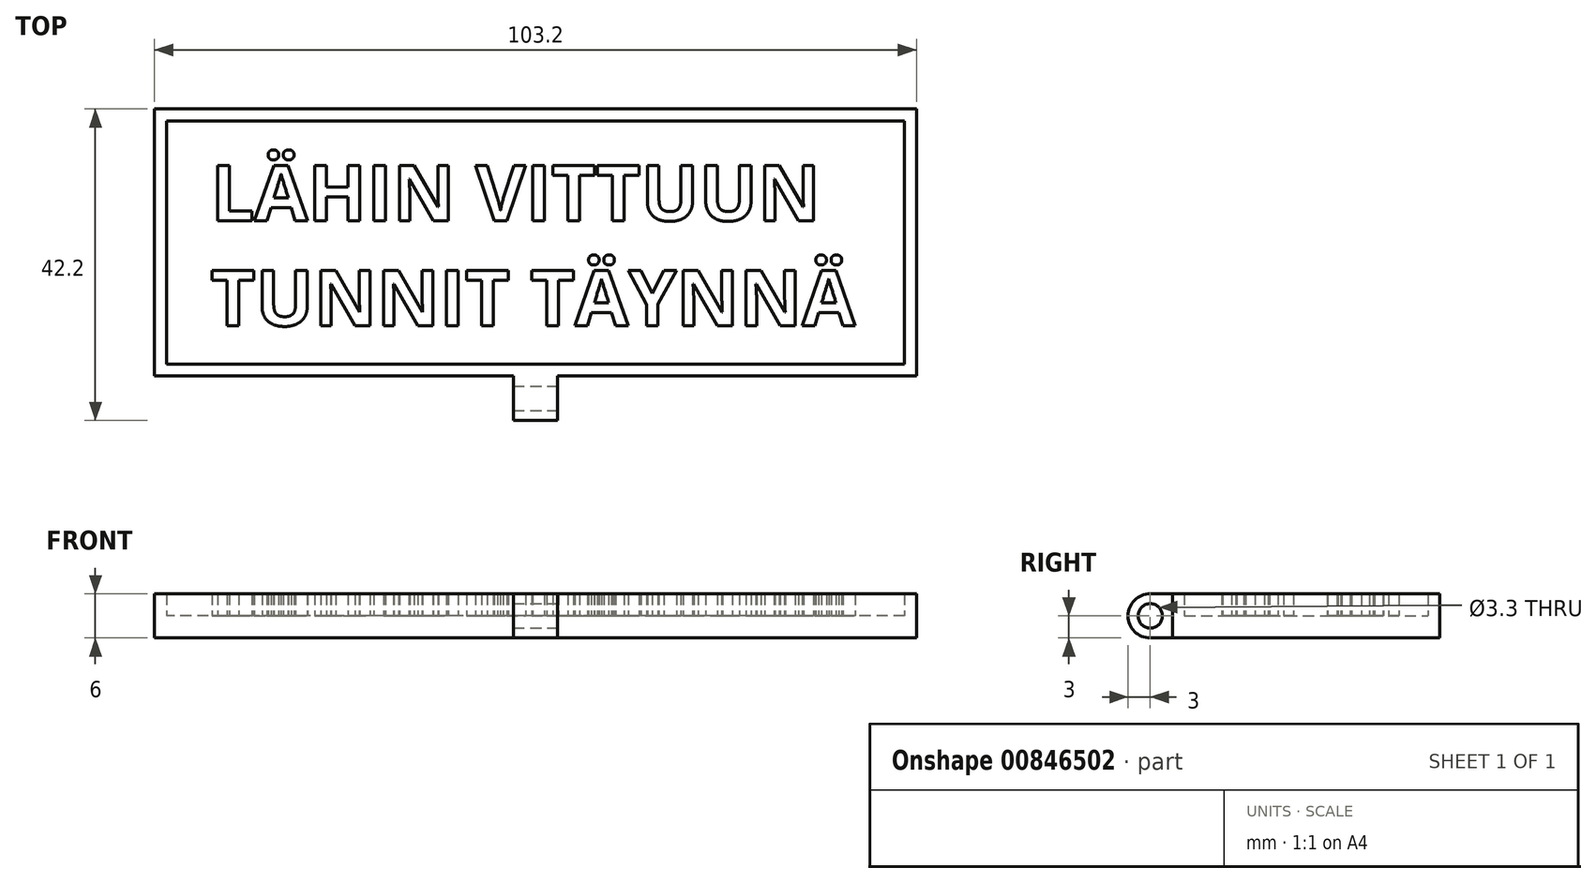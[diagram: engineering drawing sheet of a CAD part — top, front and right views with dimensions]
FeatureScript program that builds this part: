
annotation { "Feature Type Name" : "Feature", "Feature Type Description" : "" }
export const myFeature = defineFeature(function(context is Context, id is Id, definition is map)
    precondition{}
    {
        {
            var Q0;
            Q0=qCreatedBy(makeId("Top.planeOp"),FACE);
            var sketch = newSketch(context, id + "F0", { "sketchPlane" : qUnion([Q0])});
            skText(sketch, "E0", { "text": "LÄHIN VITTUUN\nTUNNIT TÄYNNÄ", "fontName": "OpenSans-Bold.ttf"});
            skLineSegment(sketch, "E1.bottom", {"start": v(0, 0) * mm, "end": v(100, 0) * mm});
            skLineSegment(sketch, "E1.top", {"start": v(0, -33) * mm, "end": v(100, -33) * mm});
            skLineSegment(sketch, "E1.left", {"start": v(0, 0) * mm, "end": v(0, -33) * mm});
            skLineSegment(sketch, "E1.right", {"start": v(100, 0) * mm, "end": v(100, -33) * mm});
            skLineSegment(sketch, "E2.0", {"start": v(-1.6, 1.6) * mm, "end": v(-1.6, -34.6) * mm});
            skLineSegment(sketch, "E2.1", {"start": v(-1.6, 1.6) * mm, "end": v(101.6, 1.6) * mm});
            skLineSegment(sketch, "E2.2", {"start": v(101.6, 1.6) * mm, "end": v(101.6, -34.6) * mm});
            skLineSegment(sketch, "E2.3", {"start": v(-1.6, -34.6) * mm, "end": v(101.6, -34.6) * mm});
            const initialGuessF0  = {"E0": [0.006, -0.01354, 1, 0, 0.00754]};
            skSetInitialGuess(sketch, initialGuessF0);
            skSolve(sketch);
        }
        {
            var Q0;
            Q0=makeQuery(id+"F0.imprint","IMPRINT",FACE,{"disambiguationData":[TD([[makeQuery(id+"F0.imprint","IMPRINT",EDGE,{"derivedFrom":sQuery(id+"F0.wireOp",EDGE,"E1.bottom")}),1.0]])]});
            var Q1;
            Q1=makeQuery(id+"F0.imprint","IMPRINT",FACE,{"disambiguationData":[TD([[makeQuery(id+"F0.imprint","IMPRINT",EDGE,{"derivedFrom":sQuery(id+"F0.wireOp",EDGE,"E0.sketch_text.stroke-0")}),-1.0]])]});
            var Q2;
            Q2=makeQuery(id+"F0.imprint","IMPRINT",FACE,{"disambiguationData":[TD([[makeQuery(id+"F0.imprint","IMPRINT",EDGE,{"derivedFrom":sQuery(id+"F0.wireOp",EDGE,"E0.sketch_text.stroke-0")}),1.0]])]});
            var Q3;
            Q3=makeQuery(id+"F0.imprint","IMPRINT",FACE,{"disambiguationData":[TD([[makeQuery(id+"F0.imprint","IMPRINT",EDGE,{"derivedFrom":sQuery(id+"F0.wireOp",EDGE,"E0.sketch_text.stroke-109")}),-1.0]])]});
            var Q4;
            Q4=makeQuery(id+"F0.imprint","IMPRINT",FACE,{"disambiguationData":[TD([[makeQuery(id+"F0.imprint","IMPRINT",EDGE,{"derivedFrom":sQuery(id+"F0.wireOp",EDGE,"E0.sketch_text.stroke-86")}),-1.0]])]});
            var Q5;
            Q5=makeQuery(id+"F0.imprint","IMPRINT",FACE,{"disambiguationData":[TD([[makeQuery(id+"F0.imprint","IMPRINT",EDGE,{"derivedFrom":sQuery(id+"F0.wireOp",EDGE,"E0.sketch_text.stroke-78")}),-1.0]])]});
            var Q6;
            Q6=makeQuery(id+"F0.imprint","IMPRINT",FACE,{"disambiguationData":[TD([[makeQuery(id+"F0.imprint","IMPRINT",EDGE,{"derivedFrom":sQuery(id+"F0.wireOp",EDGE,"E0.sketch_text.stroke-64")}),-1.0]])]});
            var Q7;
            Q7=makeQuery(id+"F0.imprint","IMPRINT",FACE,{"disambiguationData":[TD([[makeQuery(id+"F0.imprint","IMPRINT",EDGE,{"derivedFrom":sQuery(id+"F0.wireOp",EDGE,"E0.sketch_text.stroke-94")}),-1.0]])]});
            var Q8;
            Q8=makeQuery(id+"F0.imprint","IMPRINT",FACE,{"disambiguationData":[TD([[makeQuery(id+"F0.imprint","IMPRINT",EDGE,{"derivedFrom":sQuery(id+"F0.wireOp",EDGE,"E0.sketch_text.stroke-74")}),-1.0]])]});
            var Q9;
            Q9=makeQuery(id+"F0.imprint","IMPRINT",FACE,{"disambiguationData":[TD([[makeQuery(id+"F0.imprint","IMPRINT",EDGE,{"derivedFrom":sQuery(id+"F0.wireOp",EDGE,"E0.sketch_text.stroke-6")}),-1.0]])]});
            var Q10;
            Q10=makeQuery(id+"F0.imprint","IMPRINT",FACE,{"disambiguationData":[TD([[makeQuery(id+"F0.imprint","IMPRINT",EDGE,{"derivedFrom":sQuery(id+"F0.wireOp",EDGE,"E0.sketch_text.stroke-146")}),-1.0]])]});
            var Q11;
            Q11=makeQuery(id+"F0.imprint","IMPRINT",FACE,{"disambiguationData":[TD([[makeQuery(id+"F0.imprint","IMPRINT",EDGE,{"derivedFrom":sQuery(id+"F0.wireOp",EDGE,"E0.sketch_text.stroke-18")}),-1.0]])]});
            var Q12;
            Q12=makeQuery(id+"F0.imprint","IMPRINT",FACE,{"disambiguationData":[TD([[makeQuery(id+"F0.imprint","IMPRINT",EDGE,{"derivedFrom":sQuery(id+"F0.wireOp",EDGE,"E0.sketch_text.stroke-246")}),-1.0]])]});
            var Q13;
            Q13=makeQuery(id+"F0.imprint","IMPRINT",FACE,{"disambiguationData":[TD([[makeQuery(id+"F0.imprint","IMPRINT",EDGE,{"derivedFrom":sQuery(id+"F0.wireOp",EDGE,"E0.sketch_text.stroke-14")}),1.0]])]});
            var Q14;
            Q14=makeQuery(id+"F0.imprint","IMPRINT",FACE,{"disambiguationData":[TD([[makeQuery(id+"F0.imprint","IMPRINT",EDGE,{"derivedFrom":sQuery(id+"F0.wireOp",EDGE,"E0.sketch_text.stroke-34")}),-1.0]])]});
            var Q15;
            Q15=makeQuery(id+"F0.imprint","IMPRINT",FACE,{"disambiguationData":[TD([[makeQuery(id+"F0.imprint","IMPRINT",EDGE,{"derivedFrom":sQuery(id+"F0.wireOp",EDGE,"E0.sketch_text.stroke-46")}),-1.0]])]});
            var Q16;
            Q16=makeQuery(id+"F0.imprint","IMPRINT",FACE,{"disambiguationData":[TD([[makeQuery(id+"F0.imprint","IMPRINT",EDGE,{"derivedFrom":sQuery(id+"F0.wireOp",EDGE,"E0.sketch_text.stroke-286")}),-1.0]])]});
            var Q17;
            Q17=makeQuery(id+"F0.imprint","IMPRINT",FACE,{"disambiguationData":[TD([[makeQuery(id+"F0.imprint","IMPRINT",EDGE,{"derivedFrom":sQuery(id+"F0.wireOp",EDGE,"E0.sketch_text.stroke-282")}),1.0]])]});
            var Q18;
            Q18=makeQuery(id+"F0.imprint","IMPRINT",FACE,{"disambiguationData":[TD([[makeQuery(id+"F0.imprint","IMPRINT",EDGE,{"derivedFrom":sQuery(id+"F0.wireOp",EDGE,"E0.sketch_text.stroke-50")}),-1.0]])]});
            var Q19;
            Q19=makeQuery(id+"F0.imprint","IMPRINT",FACE,{"disambiguationData":[TD([[makeQuery(id+"F0.imprint","IMPRINT",EDGE,{"derivedFrom":sQuery(id+"F0.wireOp",EDGE,"E0.sketch_text.stroke-221")}),-1.0]])]});
            var Q20;
            Q20=makeQuery(id+"F0.imprint","IMPRINT",FACE,{"disambiguationData":[TD([[makeQuery(id+"F0.imprint","IMPRINT",EDGE,{"derivedFrom":sQuery(id+"F0.wireOp",EDGE,"E0.sketch_text.stroke-189")}),-1.0]])]});
            var Q21;
            Q21=makeQuery(id+"F0.imprint","IMPRINT",FACE,{"disambiguationData":[TD([[makeQuery(id+"F0.imprint","IMPRINT",EDGE,{"derivedFrom":sQuery(id+"F0.wireOp",EDGE,"E0.sketch_text.stroke-260")}),-1.0]])]});
            var Q22;
            Q22=makeQuery(id+"F0.imprint","IMPRINT",FACE,{"disambiguationData":[TD([[makeQuery(id+"F0.imprint","IMPRINT",EDGE,{"derivedFrom":sQuery(id+"F0.wireOp",EDGE,"E0.sketch_text.stroke-274")}),-1.0]])]});
            var Q23;
            Q23=makeQuery(id+"F0.imprint","IMPRINT",FACE,{"disambiguationData":[TD([[makeQuery(id+"F0.imprint","IMPRINT",EDGE,{"derivedFrom":sQuery(id+"F0.wireOp",EDGE,"E0.sketch_text.stroke-237")}),-1.0]])]});
            var Q24;
            Q24=makeQuery(id+"F0.imprint","IMPRINT",FACE,{"disambiguationData":[TD([[makeQuery(id+"F0.imprint","IMPRINT",EDGE,{"derivedFrom":sQuery(id+"F0.wireOp",EDGE,"E0.sketch_text.stroke-124")}),-1.0]])]});
            var Q25;
            Q25=makeQuery(id+"F0.imprint","IMPRINT",FACE,{"disambiguationData":[TD([[makeQuery(id+"F0.imprint","IMPRINT",EDGE,{"derivedFrom":sQuery(id+"F0.wireOp",EDGE,"E0.sketch_text.stroke-193")}),-1.0]])]});
            var Q26;
            Q26=makeQuery(id+"F0.imprint","IMPRINT",FACE,{"disambiguationData":[TD([[makeQuery(id+"F0.imprint","IMPRINT",EDGE,{"derivedFrom":sQuery(id+"F0.wireOp",EDGE,"E0.sketch_text.stroke-229")}),-1.0]])]});
            var Q27;
            Q27=makeQuery(id+"F0.imprint","IMPRINT",FACE,{"disambiguationData":[TD([[makeQuery(id+"F0.imprint","IMPRINT",EDGE,{"derivedFrom":sQuery(id+"F0.wireOp",EDGE,"E0.sketch_text.stroke-26")}),-1.0]])]});
            var Q28;
            Q28=makeQuery(id+"F0.imprint","IMPRINT",FACE,{"disambiguationData":[TD([[makeQuery(id+"F0.imprint","IMPRINT",EDGE,{"derivedFrom":sQuery(id+"F0.wireOp",EDGE,"E0.sketch_text.stroke-175")}),-1.0]])]});
            var Q29;
            Q29=makeQuery(id+"F0.imprint","IMPRINT",FACE,{"disambiguationData":[TD([[makeQuery(id+"F0.imprint","IMPRINT",EDGE,{"derivedFrom":sQuery(id+"F0.wireOp",EDGE,"E0.sketch_text.stroke-161")}),-1.0]])]});
            var Q30;
            Q30=makeQuery(id+"F0.imprint","IMPRINT",FACE,{"disambiguationData":[TD([[makeQuery(id+"F0.imprint","IMPRINT",EDGE,{"derivedFrom":sQuery(id+"F0.wireOp",EDGE,"E0.sketch_text.stroke-217")}),1.0]])]});
            var Q31;
            Q31=makeQuery(id+"F0.imprint","IMPRINT",FACE,{"disambiguationData":[TD([[makeQuery(id+"F0.imprint","IMPRINT",EDGE,{"derivedFrom":sQuery(id+"F0.wireOp",EDGE,"E0.sketch_text.stroke-201")}),-1.0]])]});
            var Q32;
            Q32=makeQuery(id+"F0.imprint","IMPRINT",FACE,{"disambiguationData":[TD([[makeQuery(id+"F0.imprint","IMPRINT",EDGE,{"derivedFrom":sQuery(id+"F0.wireOp",EDGE,"E0.sketch_text.stroke-209")}),-1.0]])]});
            var Q33;
            Q33=makeQuery(id+"F0.imprint","IMPRINT",FACE,{"disambiguationData":[TD([[makeQuery(id+"F0.imprint","IMPRINT",EDGE,{"derivedFrom":sQuery(id+"F0.wireOp",EDGE,"E0.sketch_text.stroke-138")}),-1.0]])]});
            var Q34;
            Q34=makeQuery(id+"F0.imprint","IMPRINT",FACE,{"disambiguationData":[TD([[makeQuery(id+"F0.imprint","IMPRINT",EDGE,{"derivedFrom":sQuery(id+"F0.wireOp",EDGE,"E0.sketch_text.stroke-294")}),-1.0]])]});
            extrude(context, id + "F1", {"entities" : qUnion([Q0, Q1, Q2, Q3, Q4, Q5, Q6, Q7, Q8, Q9, Q10, Q11, Q12, Q13, Q14, Q15, Q16, Q17, Q18, Q19, Q20, Q21, Q22, Q23, Q24, Q25, Q26, Q27, Q28, Q29, Q30, Q31, Q32, Q33, Q34]), "depth" : 3 * mm, "offsetDistance" : 25 * mm});
        }
        {
            var Q0;
            Q0=makeQuery(id+"F0.imprint","IMPRINT",FACE,{"disambiguationData":[TD([[makeQuery(id+"F0.imprint","IMPRINT",EDGE,{"derivedFrom":sQuery(id+"F0.wireOp",EDGE,"E1.bottom")}),1.0]])]});
            var Q1;
            Q1=makeQuery(id+"F0.imprint","IMPRINT",FACE,{"disambiguationData":[TD([[makeQuery(id+"F0.imprint","IMPRINT",EDGE,{"derivedFrom":sQuery(id+"F0.wireOp",EDGE,"E0.sketch_text.stroke-6")}),-1.0]])]});
            var Q2;
            Q2=makeQuery(id+"F0.imprint","IMPRINT",FACE,{"disambiguationData":[TD([[makeQuery(id+"F0.imprint","IMPRINT",EDGE,{"derivedFrom":sQuery(id+"F0.wireOp",EDGE,"E0.sketch_text.stroke-146")}),-1.0]])]});
            var Q3;
            Q3=makeQuery(id+"F0.imprint","IMPRINT",FACE,{"disambiguationData":[TD([[makeQuery(id+"F0.imprint","IMPRINT",EDGE,{"derivedFrom":sQuery(id+"F0.wireOp",EDGE,"E0.sketch_text.stroke-18")}),-1.0]])]});
            var Q4;
            Q4=makeQuery(id+"F0.imprint","IMPRINT",FACE,{"disambiguationData":[TD([[makeQuery(id+"F0.imprint","IMPRINT",EDGE,{"derivedFrom":sQuery(id+"F0.wireOp",EDGE,"E0.sketch_text.stroke-294")}),-1.0]])]});
            var Q5;
            Q5=makeQuery(id+"F0.imprint","IMPRINT",FACE,{"disambiguationData":[TD([[makeQuery(id+"F0.imprint","IMPRINT",EDGE,{"derivedFrom":sQuery(id+"F0.wireOp",EDGE,"E0.sketch_text.stroke-246")}),-1.0]])]});
            var Q6;
            Q6=makeQuery(id+"F0.imprint","IMPRINT",FACE,{"disambiguationData":[TD([[makeQuery(id+"F0.imprint","IMPRINT",EDGE,{"derivedFrom":sQuery(id+"F0.wireOp",EDGE,"E0.sketch_text.stroke-34")}),-1.0]])]});
            var Q7;
            Q7=makeQuery(id+"F0.imprint","IMPRINT",FACE,{"disambiguationData":[TD([[makeQuery(id+"F0.imprint","IMPRINT",EDGE,{"derivedFrom":sQuery(id+"F0.wireOp",EDGE,"E0.sketch_text.stroke-46")}),-1.0]])]});
            var Q8;
            Q8=makeQuery(id+"F0.imprint","IMPRINT",FACE,{"disambiguationData":[TD([[makeQuery(id+"F0.imprint","IMPRINT",EDGE,{"derivedFrom":sQuery(id+"F0.wireOp",EDGE,"E0.sketch_text.stroke-286")}),-1.0]])]});
            var Q9;
            Q9=makeQuery(id+"F0.imprint","IMPRINT",FACE,{"disambiguationData":[TD([[makeQuery(id+"F0.imprint","IMPRINT",EDGE,{"derivedFrom":sQuery(id+"F0.wireOp",EDGE,"E0.sketch_text.stroke-109")}),-1.0]])]});
            var Q10;
            Q10=makeQuery(id+"F0.imprint","IMPRINT",FACE,{"disambiguationData":[TD([[makeQuery(id+"F0.imprint","IMPRINT",EDGE,{"derivedFrom":sQuery(id+"F0.wireOp",EDGE,"E0.sketch_text.stroke-50")}),-1.0]])]});
            var Q11;
            Q11=makeQuery(id+"F0.imprint","IMPRINT",FACE,{"disambiguationData":[TD([[makeQuery(id+"F0.imprint","IMPRINT",EDGE,{"derivedFrom":sQuery(id+"F0.wireOp",EDGE,"E0.sketch_text.stroke-86")}),-1.0]])]});
            var Q12;
            Q12=makeQuery(id+"F0.imprint","IMPRINT",FACE,{"disambiguationData":[TD([[makeQuery(id+"F0.imprint","IMPRINT",EDGE,{"derivedFrom":sQuery(id+"F0.wireOp",EDGE,"E0.sketch_text.stroke-78")}),-1.0]])]});
            var Q13;
            Q13=makeQuery(id+"F0.imprint","IMPRINT",FACE,{"disambiguationData":[TD([[makeQuery(id+"F0.imprint","IMPRINT",EDGE,{"derivedFrom":sQuery(id+"F0.wireOp",EDGE,"E0.sketch_text.stroke-221")}),-1.0]])]});
            var Q14;
            Q14=makeQuery(id+"F0.imprint","IMPRINT",FACE,{"disambiguationData":[TD([[makeQuery(id+"F0.imprint","IMPRINT",EDGE,{"derivedFrom":sQuery(id+"F0.wireOp",EDGE,"E0.sketch_text.stroke-189")}),-1.0]])]});
            var Q15;
            Q15=makeQuery(id+"F0.imprint","IMPRINT",FACE,{"disambiguationData":[TD([[makeQuery(id+"F0.imprint","IMPRINT",EDGE,{"derivedFrom":sQuery(id+"F0.wireOp",EDGE,"E0.sketch_text.stroke-260")}),-1.0]])]});
            var Q16;
            Q16=makeQuery(id+"F0.imprint","IMPRINT",FACE,{"disambiguationData":[TD([[makeQuery(id+"F0.imprint","IMPRINT",EDGE,{"derivedFrom":sQuery(id+"F0.wireOp",EDGE,"E0.sketch_text.stroke-274")}),-1.0]])]});
            var Q17;
            Q17=makeQuery(id+"F0.imprint","IMPRINT",FACE,{"disambiguationData":[TD([[makeQuery(id+"F0.imprint","IMPRINT",EDGE,{"derivedFrom":sQuery(id+"F0.wireOp",EDGE,"E0.sketch_text.stroke-64")}),-1.0]])]});
            var Q18;
            Q18=makeQuery(id+"F0.imprint","IMPRINT",FACE,{"disambiguationData":[TD([[makeQuery(id+"F0.imprint","IMPRINT",EDGE,{"derivedFrom":sQuery(id+"F0.wireOp",EDGE,"E0.sketch_text.stroke-237")}),-1.0]])]});
            var Q19;
            Q19=makeQuery(id+"F0.imprint","IMPRINT",FACE,{"disambiguationData":[TD([[makeQuery(id+"F0.imprint","IMPRINT",EDGE,{"derivedFrom":sQuery(id+"F0.wireOp",EDGE,"E0.sketch_text.stroke-124")}),-1.0]])]});
            var Q20;
            Q20=makeQuery(id+"F0.imprint","IMPRINT",FACE,{"disambiguationData":[TD([[makeQuery(id+"F0.imprint","IMPRINT",EDGE,{"derivedFrom":sQuery(id+"F0.wireOp",EDGE,"E0.sketch_text.stroke-193")}),-1.0]])]});
            var Q21;
            Q21=makeQuery(id+"F0.imprint","IMPRINT",FACE,{"disambiguationData":[TD([[makeQuery(id+"F0.imprint","IMPRINT",EDGE,{"derivedFrom":sQuery(id+"F0.wireOp",EDGE,"E0.sketch_text.stroke-94")}),-1.0]])]});
            var Q22;
            Q22=makeQuery(id+"F0.imprint","IMPRINT",FACE,{"disambiguationData":[TD([[makeQuery(id+"F0.imprint","IMPRINT",EDGE,{"derivedFrom":sQuery(id+"F0.wireOp",EDGE,"E0.sketch_text.stroke-229")}),-1.0]])]});
            var Q23;
            Q23=makeQuery(id+"F0.imprint","IMPRINT",FACE,{"disambiguationData":[TD([[makeQuery(id+"F0.imprint","IMPRINT",EDGE,{"derivedFrom":sQuery(id+"F0.wireOp",EDGE,"E0.sketch_text.stroke-26")}),-1.0]])]});
            var Q24;
            Q24=makeQuery(id+"F0.imprint","IMPRINT",FACE,{"disambiguationData":[TD([[makeQuery(id+"F0.imprint","IMPRINT",EDGE,{"derivedFrom":sQuery(id+"F0.wireOp",EDGE,"E0.sketch_text.stroke-175")}),-1.0]])]});
            var Q25;
            Q25=makeQuery(id+"F0.imprint","IMPRINT",FACE,{"disambiguationData":[TD([[makeQuery(id+"F0.imprint","IMPRINT",EDGE,{"derivedFrom":sQuery(id+"F0.wireOp",EDGE,"E0.sketch_text.stroke-161")}),-1.0]])]});
            var Q26;
            Q26=makeQuery(id+"F0.imprint","IMPRINT",FACE,{"disambiguationData":[TD([[makeQuery(id+"F0.imprint","IMPRINT",EDGE,{"derivedFrom":sQuery(id+"F0.wireOp",EDGE,"E0.sketch_text.stroke-201")}),-1.0]])]});
            var Q27;
            Q27=makeQuery(id+"F0.imprint","IMPRINT",FACE,{"disambiguationData":[TD([[makeQuery(id+"F0.imprint","IMPRINT",EDGE,{"derivedFrom":sQuery(id+"F0.wireOp",EDGE,"E0.sketch_text.stroke-209")}),-1.0]])]});
            var Q28;
            Q28=makeQuery(id+"F0.imprint","IMPRINT",FACE,{"disambiguationData":[TD([[makeQuery(id+"F0.imprint","IMPRINT",EDGE,{"derivedFrom":sQuery(id+"F0.wireOp",EDGE,"E0.sketch_text.stroke-74")}),-1.0]])]});
            var Q29;
            Q29=makeQuery(id+"F0.imprint","IMPRINT",FACE,{"disambiguationData":[TD([[makeQuery(id+"F0.imprint","IMPRINT",EDGE,{"derivedFrom":sQuery(id+"F0.wireOp",EDGE,"E0.sketch_text.stroke-0")}),-1.0]])]});
            var Q30;
            Q30=makeQuery(id+"F0.imprint","IMPRINT",FACE,{"disambiguationData":[TD([[makeQuery(id+"F0.imprint","IMPRINT",EDGE,{"derivedFrom":sQuery(id+"F0.wireOp",EDGE,"E0.sketch_text.stroke-138")}),-1.0]])]});
            extrude(context, id + "F2", {"entities" : qUnion([Q0, Q1, Q2, Q3, Q4, Q5, Q6, Q7, Q8, Q9, Q10, Q11, Q12, Q13, Q14, Q15, Q16, Q17, Q18, Q19, Q20, Q21, Q22, Q23, Q24, Q25, Q26, Q27, Q28, Q29, Q30]), "operationType" : NewBodyOperationType.ADD, "depth" : 6 * mm, "offsetDistance" : 25 * mm});
        }
        {
            var Q0;
            {var subQ0=sQuery(id+"F0.wireOp",EDGE,"E2.3");Q0=makeQuery(id+"F2.boolean.opBoolean","MERGE",FACE,{"derivedFrom":[makeQuery(id+"F1.opExtrude","SWEPT_FACE",FACE,{"disambiguationData":[OSD([subQ0])]}),makeQuery(id+"F2.opExtrude","SWEPT_FACE",FACE,{"disambiguationData":[OSD([subQ0])]})]});}
            var sketch = newSketch(context, id + "F3", { "sketchPlane" : qUnion([Q0])});
            skLineSegment(sketch, "E3", {"start": v(-1.6, 0) * mm, "end": v(101.6, 6) * mm, "construction": true});
            skLineSegment(sketch, "E4.bottom", {"start": v(47, 0) * mm, "end": v(53, 0) * mm});
            skLineSegment(sketch, "E4.top", {"start": v(47, 6) * mm, "end": v(53, 6) * mm});
            skLineSegment(sketch, "E4.left", {"start": v(47, 0) * mm, "end": v(47, 6) * mm});
            skLineSegment(sketch, "E4.right", {"start": v(53, 0) * mm, "end": v(53, 6) * mm});
            skPoint(sketch, "E4.middle", {"position": v(50, 3) * mm});
            skSolve(sketch);
        }
        {
            var Q0;
            Q0=makeQuery(id+"F3.imprint","IMPRINT",FACE,{"disambiguationData":[TD([[makeQuery(id+"F3.imprint","IMPRINT",EDGE,{"derivedFrom":sQuery(id+"F3.wireOp",EDGE,"E4.bottom")}),1.0]])]});
            extrude(context, id + "F4", {"entities" : qUnion([Q0]), "operationType" : NewBodyOperationType.ADD, "depth" : 6 * mm, "offsetDistance" : 25 * mm});
        }
        {
            var Q0;
            Q0=makeQuery(id+"F4.opExtrude","SWEPT_FACE",FACE,{"disambiguationData":[OSD([sQuery(id+"F3.wireOp",EDGE,"E4.right")])]});
            var sketch = newSketch(context, id + "F5", { "sketchPlane" : qUnion([Q0])});
            skLineSegment(sketch, "E5", {"start": v(-40.6, 0) * mm, "end": v(-34.6, 6) * mm, "construction": true});
            skCircle(sketch, "E6", {"center": v(-37.6, 3) * mm, "radius": 1.65 * mm});
            skSolve(sketch);
        }
        {
            var Q0;
            Q0 = qSketchRegion(id + "F5", true);
            extrude(context, id + "F6", {"entities" : qUnion([Q0]), "operationType" : NewBodyOperationType.REMOVE, "oppositeDirection" : true, "depth" : 25 * mm, "offsetDistance" : 25 * mm});
        }
        {
            var Q0;
            Q0=makeQuery(id+"F4.opExtrude","CAP_EDGE",EDGE,{"disambiguationData":[OSD([sQuery(id+"F3.wireOp",EDGE,"E4.top")])],"isStart":false});
            var Q1;
            Q1=makeQuery(id+"F4.opExtrude","CAP_EDGE",EDGE,{"disambiguationData":[OSD([sQuery(id+"F3.wireOp",EDGE,"E4.bottom")])],"isStart":false});
            fillet(context, id + "F7", {"entities" : qUnion([Q0, Q1]), "radius" : 3 * mm, "tangentPropagation" : true, "allowEdgeOverflow" : false});
        }
    });
